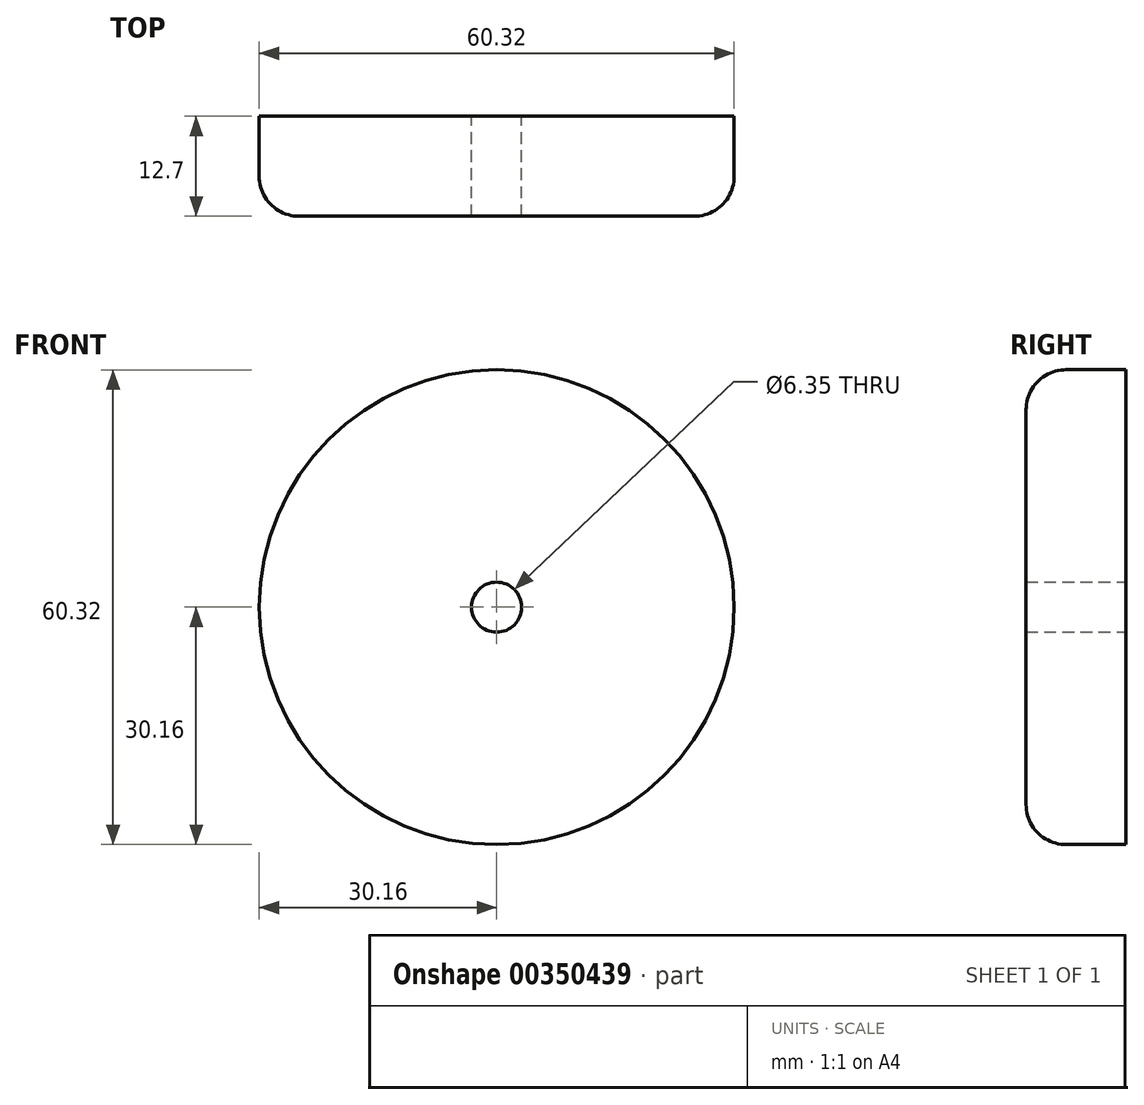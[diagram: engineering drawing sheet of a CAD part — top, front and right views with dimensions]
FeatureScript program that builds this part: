
annotation { "Feature Type Name" : "Feature", "Feature Type Description" : "" }
export const myFeature = defineFeature(function(context is Context, id is Id, definition is map)
    precondition{}
    {
        {
            var Q0;
            Q0=qCreatedBy(makeId("Front.planeOp"),FACE);
            var sketch = newSketch(context, id + "F0", { "sketchPlane" : qUnion([Q0])});
            skCircle(sketch, "E0", {"center": v(0, 0) * mm, "radius": 30.16 * mm});
            skCircle(sketch, "E1", {"center": v(0, 0) * mm, "radius": 3.18 * mm});
            skSolve(sketch);
        }
        {
            var Q0;
            Q0=makeQuery(id+"F0.imprint","IMPRINT",FACE,{"disambiguationData":[TD([[makeQuery(id+"F0.imprint","IMPRINT",EDGE,{"derivedFrom":sQuery(id+"F0.wireOp",EDGE,"E0")}),1.0]])]});
            var Q1;
            Q1=makeQuery(id+"F0.imprint","IMPRINT",FACE,{"disambiguationData":[TD([[makeQuery(id+"F0.imprint","IMPRINT",EDGE,{"derivedFrom":sQuery(id+"F0.wireOp",EDGE,"E1")}),-1.0]])]});
            extrude(context, id + "F1", {"entities" : qUnion([Q0, Q1]), "endBound" : BoundingType.SYMMETRIC, "depth" : 12.7 * mm});
        }
        {
            var Q0;
            Q0=makeQuery(id+"F1.opExtrude","CAP_EDGE",EDGE,{"disambiguationData":[OSD([sQuery(id+"F0.wireOp",EDGE,"E0")])],"isStart":false});
            fillet(context, id + "F2", {"entities" : qUnion([Q0]), "radius" : 5.08 * mm, "tangentPropagation" : true, "allowEdgeOverflow" : false});
        }
    });
